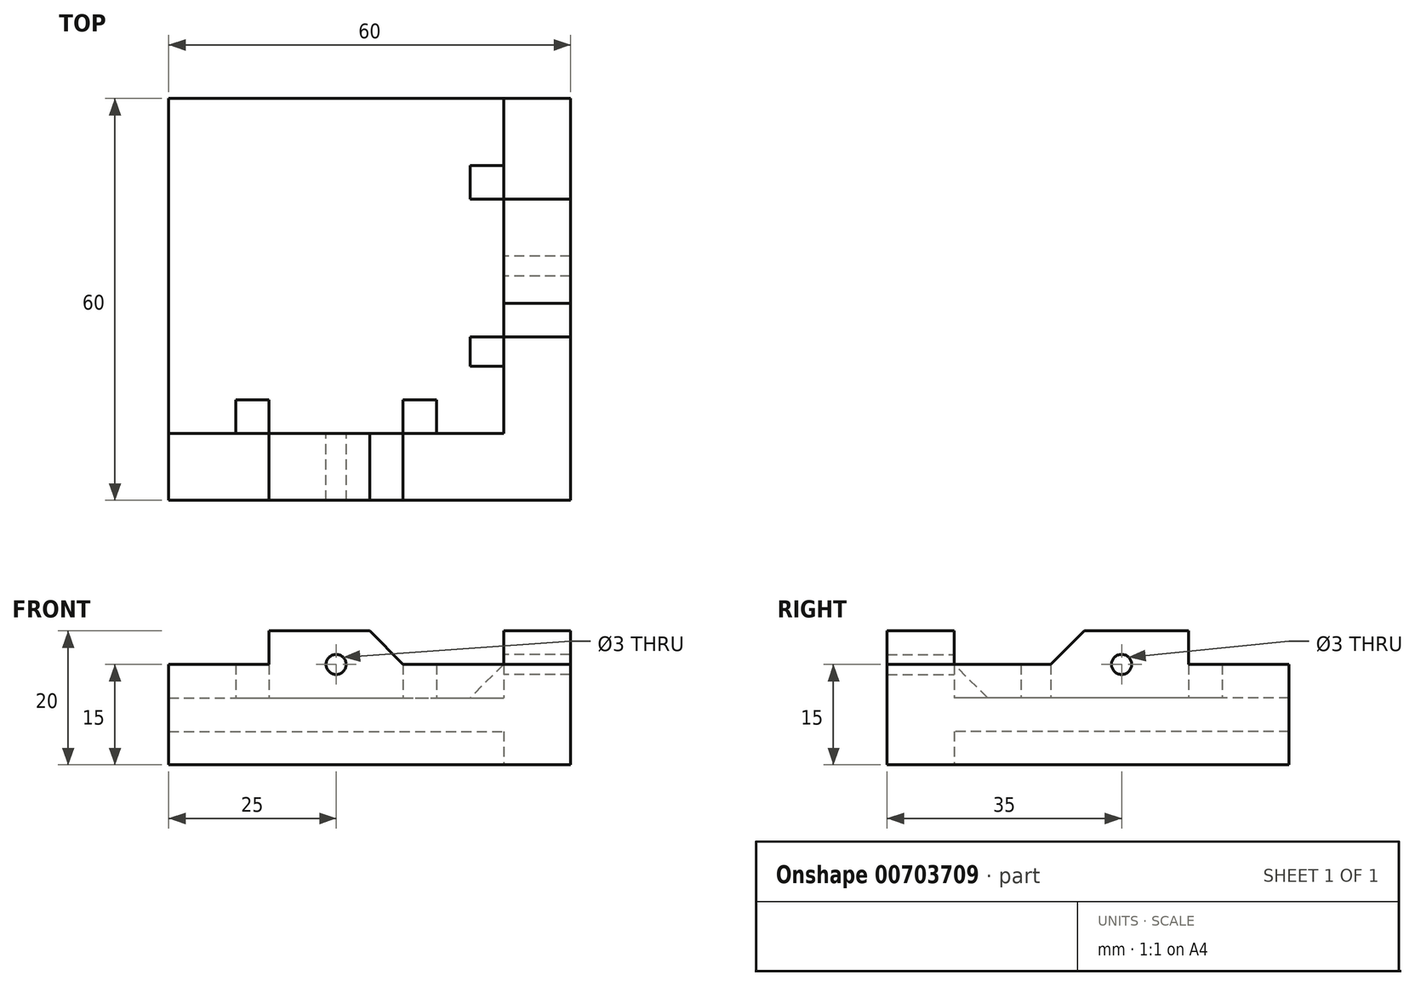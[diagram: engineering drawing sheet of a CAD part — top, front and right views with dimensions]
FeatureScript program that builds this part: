
annotation { "Feature Type Name" : "Feature", "Feature Type Description" : "" }
export const myFeature = defineFeature(function(context is Context, id is Id, definition is map)
    precondition{}
    {
        {
            var Q0;
            Q0=qCreatedBy(makeId("Top.planeOp"),FACE);
            var sketch = newSketch(context, id + "F0", { "sketchPlane" : qUnion([Q0])});
            skLineSegment(sketch, "E0", {"start": v(0, 0) * mm, "end": v(50, 0) * mm});
            skLineSegment(sketch, "E1", {"start": v(50, 0) * mm, "end": v(50, 50) * mm});
            skLineSegment(sketch, "E2.0", {"start": v(60, -10) * mm, "end": v(60, 50) * mm});
            skLineSegment(sketch, "E2.1", {"start": v(0, -10) * mm, "end": v(60, -10) * mm});
            skLineSegment(sketch, "E3", {"start": v(50, 50) * mm, "end": v(60, 50) * mm});
            skLineSegment(sketch, "E4", {"start": v(0, 0) * mm, "end": v(0, -10) * mm});
            skSolve(sketch);
        }
        {
            var Q0;
            Q0=makeQuery(id+"F0.imprint","IMPRINT",FACE,{"disambiguationData":[TD([[makeQuery(id+"F0.imprint","IMPRINT",EDGE,{"derivedFrom":sQuery(id+"F0.wireOp",EDGE,"E0")}),-1.0]])]});
            extrude(context, id + "F1", {"entities" : qUnion([Q0]), "depth" : 15 * mm, "offsetDistance" : 25 * mm});
        }
        {
            var Q0;
            Q0=makeQuery(id+"F1.opExtrude","SWEPT_FACE",FACE,{"disambiguationData":[OSD([sQuery(id+"F0.wireOp",EDGE,"E1")])]});
            var sketch = newSketch(context, id + "F2", { "sketchPlane" : qUnion([Q0])});
            skLineSegment(sketch, "E5", {"start": v(-50, 0) * mm, "end": v(-50, 5) * mm});
            skLineSegment(sketch, "E6", {"start": v(-50, 5) * mm, "end": v(0, 5) * mm});
            skLineSegment(sketch, "E7.0", {"start": v(-50, 10) * mm, "end": v(0, 10) * mm});
            skLineSegment(sketch, "E8", {"start": v(-50, 15) * mm, "end": v(-37.5, 15) * mm});
            skLineSegment(sketch, "E9", {"start": v(0, 15) * mm, "end": v(-12.5, 15) * mm});
            skLineSegment(sketch, "E10", {"start": v(-37.5, 15) * mm, "end": v(-35, 15) * mm});
            skLineSegment(sketch, "E11", {"start": v(-35, 15) * mm, "end": v(-35, 10) * mm});
            skLineSegment(sketch, "E12.0", {"start": v(-40, 15) * mm, "end": v(-40, 10) * mm});
            skLineSegment(sketch, "E13.0", {"start": v(-10, 15) * mm, "end": v(-10, 10) * mm});
            skLineSegment(sketch, "E14.0", {"start": v(-14.42, 15) * mm, "end": v(-14.42, 10) * mm});
            skLineSegment(sketch, "E15", {"start": v(-35, 15) * mm, "end": v(-35, 20) * mm});
            skLineSegment(sketch, "E16", {"start": v(-35, 20) * mm, "end": v(-19.42, 20) * mm});
            skLineSegment(sketch, "E17", {"start": v(-19.42, 20) * mm, "end": v(-14.42, 15) * mm});
            skCircle(sketch, "E18", {"center": v(-25, 15) * mm, "radius": 1.5 * mm});
            skSolve(sketch);
        }
        {
            var Q0;
            {var subQ0=sQuery(id+"F2.wireOp",EDGE,"E6");Q0=makeQuery(id+"F2.imprint","IMPRINT",FACE,{"disambiguationData":[TD([[makeQuery(id+"F2.imprint","IMPRINT",EDGE,{"derivedFrom":subQ0}),1.0]])]});}
            extrude(context, id + "F3", {"entities" : qUnion([Q0]), "operationType" : NewBodyOperationType.ADD, "depth" : 50 * mm, "offsetDistance" : 25 * mm});
        }
        {
            var Q0;
            {var subQ0=sQuery(id+"F2.wireOp",EDGE,"E10");Q0=makeQuery(id+"F2.imprint","IMPRINT",FACE,{"disambiguationData":[TD([[makeQuery(id+"F2.imprint","IMPRINT",EDGE,{"derivedFrom":subQ0}),1.0]])]});}
            var Q1;
            {var subQ0=sQuery(id+"F2.wireOp",EDGE,"E13.0");Q1=makeQuery(id+"F2.imprint","IMPRINT",FACE,{"disambiguationData":[TD([[makeQuery(id+"F2.imprint","IMPRINT",EDGE,{"derivedFrom":subQ0}),-1.0]])]});}
            extrude(context, id + "F4", {"entities" : qUnion([Q0, Q1]), "operationType" : NewBodyOperationType.ADD, "depth" : 5 * mm, "offsetDistance" : 25 * mm});
        }
        {
            var Q0;
            Q0=makeQuery(id+"F4.opExtrude","SWEPT_FACE",FACE,{"disambiguationData":[OSD([sQuery(id+"F2.wireOp",EDGE,"E12.0")])]});
            var sketch = newSketch(context, id + "F5", { "sketchPlane" : qUnion([Q0])});
            skLineSegment(sketch, "E19", {"start": v(-50, 15) * mm, "end": v(-45, 10) * mm});
            skLineSegment(sketch, "E20", {"start": v(-45, 10) * mm, "end": v(-45, 15) * mm});
            skLineSegment(sketch, "E21", {"start": v(-45, 15) * mm, "end": v(-50, 15) * mm});
            skSolve(sketch);
        }
        {
            var Q0;
            Q0 = qSketchRegion(id + "F5", true);
            extrude(context, id + "F6", {"entities" : qUnion([Q0]), "operationType" : NewBodyOperationType.REMOVE, "oppositeDirection" : true, "depth" : 34.1 * mm, "offsetDistance" : 25 * mm});
        }
        {
            var Q0;
            {var subQ0=sQuery(id+"F2.wireOp",EDGE,"E7.0");var subQ3=sQuery(id+"F0.wireOp",EDGE,"E0");Q0=makeQuery(id+"F3.boolean.opBoolean","SPLIT",FACE,{"disambiguationData":[TD([makeQuery(id+"F3.opExtrude","SWEPT_FACE",FACE,{"disambiguationData":[OSD([subQ0])]})])],"derivedFrom":makeQuery(id+"F1.opExtrude","SWEPT_FACE",FACE,{"disambiguationData":[OSD([subQ3])]})});}
            var sketch = newSketch(context, id + "F7", { "sketchPlane" : qUnion([Q0])});
            skLineSegment(sketch, "E22", {"start": v(-50, 0) * mm, "end": v(-50, 5) * mm});
            skLineSegment(sketch, "E23", {"start": v(-50, 5) * mm, "end": v(0, 5) * mm});
            skLineSegment(sketch, "E24.0", {"start": v(-50, 10) * mm, "end": v(0, 10) * mm});
            skLineSegment(sketch, "E25", {"start": v(-50, 15) * mm, "end": v(-37.5, 15) * mm});
            skLineSegment(sketch, "E26", {"start": v(0, 15) * mm, "end": v(-12.5, 15) * mm});
            skLineSegment(sketch, "E27", {"start": v(-37.5, 15) * mm, "end": v(-35, 15) * mm});
            skLineSegment(sketch, "E28", {"start": v(-35, 15) * mm, "end": v(-35, 10) * mm});
            skLineSegment(sketch, "E29.0", {"start": v(-40, 15) * mm, "end": v(-40, 10) * mm});
            skLineSegment(sketch, "E30.0", {"start": v(-10, 15) * mm, "end": v(-10, 10) * mm});
            skLineSegment(sketch, "E31.0", {"start": v(-15, 15) * mm, "end": v(-15, 10) * mm});
            skLineSegment(sketch, "E32", {"start": v(-15, 15) * mm, "end": v(-15, 20) * mm});
            skLineSegment(sketch, "E33", {"start": v(-15, 20) * mm, "end": v(-30, 20) * mm});
            skCircle(sketch, "E34", {"center": v(-25, 15) * mm, "radius": 1.5 * mm});
            skLineSegment(sketch, "E35", {"start": v(-30, 20) * mm, "end": v(-35, 15) * mm});
            skSolve(sketch);
        }
        {
            var Q0;
            {var subQ0=sQuery(id+"F7.wireOp",EDGE,"E27");Q0=makeQuery(id+"F7.imprint","IMPRINT",FACE,{"disambiguationData":[TD([[makeQuery(id+"F7.imprint","IMPRINT",EDGE,{"derivedFrom":subQ0}),1.0]])]});}
            var Q1;
            {var subQ0=sQuery(id+"F7.wireOp",EDGE,"E30.0");Q1=makeQuery(id+"F7.imprint","IMPRINT",FACE,{"disambiguationData":[TD([[makeQuery(id+"F7.imprint","IMPRINT",EDGE,{"derivedFrom":subQ0}),-1.0]])]});}
            extrude(context, id + "F8", {"entities" : qUnion([Q0, Q1]), "operationType" : NewBodyOperationType.ADD, "depth" : 5 * mm, "offsetDistance" : 25 * mm});
        }
        {
            var Q0;
            Q0=makeQuery(id+"F8.opExtrude","SWEPT_FACE",FACE,{"disambiguationData":[OSD([sQuery(id+"F7.wireOp",EDGE,"E30.0")])]});
            var sketch = newSketch(context, id + "F9", { "sketchPlane" : qUnion([Q0])});
            skLineSegment(sketch, "E36", {"start": v(-5, 10) * mm, "end": v(0, 15) * mm});
            skLineSegment(sketch, "E37", {"start": v(0, 15) * mm, "end": v(-5, 15) * mm});
            skLineSegment(sketch, "E38", {"start": v(-5, 15) * mm, "end": v(-5, 10) * mm});
            skSolve(sketch);
        }
        {
            var Q0;
            Q0=makeQuery(id+"F9.imprint","IMPRINT",FACE,{"disambiguationData":[TD([[makeQuery(id+"F9.imprint","IMPRINT",EDGE,{"derivedFrom":sQuery(id+"F9.wireOp",EDGE,"E36")}),1.0]])]});
            extrude(context, id + "F10", {"entities" : qUnion([Q0]), "operationType" : NewBodyOperationType.REMOVE, "oppositeDirection" : true, "depth" : 37.3 * mm, "offsetDistance" : 25 * mm});
        }
        {
            var Q0;
            {var subQ0=sQuery(id+"F2.wireOp",EDGE,"E15");Q0=makeQuery(id+"F2.imprint","IMPRINT",FACE,{"disambiguationData":[TD([[makeQuery(id+"F2.imprint","IMPRINT",EDGE,{"derivedFrom":subQ0}),-1.0]])]});}
            extrude(context, id + "F11", {"entities" : qUnion([Q0]), "operationType" : NewBodyOperationType.ADD, "oppositeDirection" : true, "depth" : 10 * mm, "offsetDistance" : 25 * mm});
        }
        {
            var Q0;
            {var subQ0=sQuery(id+"F7.wireOp",EDGE,"E32");Q0=makeQuery(id+"F7.imprint","IMPRINT",FACE,{"disambiguationData":[TD([[makeQuery(id+"F7.imprint","IMPRINT",EDGE,{"derivedFrom":subQ0}),1.0]])]});}
            extrude(context, id + "F12", {"entities" : qUnion([Q0]), "operationType" : NewBodyOperationType.ADD, "oppositeDirection" : true, "depth" : 10 * mm, "offsetDistance" : 25 * mm});
        }
        {
            var Q0;
            {var subQ0=sQuery(id+"F2.wireOp",EDGE,"E18");var subQ1=makeQuery(id+"F1.opExtrude","CAP_EDGE",EDGE,{"disambiguationData":[OSD([sQuery(id+"F0.wireOp",EDGE,"E1")])],"isStart":false});var subQ2=makeQuery(id+"F2.imprint","INTERSECT",VERTEX,{"disambiguationData":[OD(0.0)],"derivedFrom":[subQ1,subQ0]});Q0=makeQuery(id+"F2.imprint","IMPRINT",FACE,{"disambiguationData":[TD([[makeQuery(id+"F2.imprint","IMPRINT",EDGE,{"disambiguationData":[TD([[subQ2,1.0]])],"derivedFrom":subQ0}),1.0]])]});}
            var Q1;
            {var subQ0=sQuery(id+"F2.wireOp",EDGE,"E18");var subQ1=makeQuery(id+"F1.opExtrude","CAP_EDGE",EDGE,{"disambiguationData":[OSD([sQuery(id+"F0.wireOp",EDGE,"E1")])],"isStart":false});var subQ2=makeQuery(id+"F2.imprint","INTERSECT",VERTEX,{"disambiguationData":[OD(0.0)],"derivedFrom":[subQ1,subQ0]});Q1=makeQuery(id+"F2.imprint","IMPRINT",FACE,{"disambiguationData":[TD([[makeQuery(id+"F2.imprint","IMPRINT",EDGE,{"disambiguationData":[TD([[subQ2,-1.0]])],"derivedFrom":subQ0}),1.0]])]});}
            extrude(context, id + "F13", {"entities" : qUnion([Q0, Q1]), "operationType" : NewBodyOperationType.REMOVE, "oppositeDirection" : true, "depth" : 25 * mm, "offsetDistance" : 25 * mm});
        }
        {
            var Q0;
            {var subQ0=sQuery(id+"F7.wireOp",EDGE,"E34");var subQ1=makeQuery(id+"F1.opExtrude","CAP_EDGE",EDGE,{"disambiguationData":[OSD([sQuery(id+"F0.wireOp",EDGE,"E0")])],"isStart":false});var subQ2=makeQuery(id+"F7.imprint","INTERSECT",VERTEX,{"disambiguationData":[OD(0.0)],"derivedFrom":[subQ1,subQ0]});Q0=makeQuery(id+"F7.imprint","IMPRINT",FACE,{"disambiguationData":[TD([[makeQuery(id+"F7.imprint","IMPRINT",EDGE,{"disambiguationData":[TD([[subQ2,-1.0]])],"derivedFrom":subQ0}),1.0]])]});}
            var Q1;
            {var subQ0=sQuery(id+"F7.wireOp",EDGE,"E34");var subQ1=makeQuery(id+"F1.opExtrude","CAP_EDGE",EDGE,{"disambiguationData":[OSD([sQuery(id+"F0.wireOp",EDGE,"E0")])],"isStart":false});var subQ2=makeQuery(id+"F7.imprint","INTERSECT",VERTEX,{"disambiguationData":[OD(0.0)],"derivedFrom":[subQ1,subQ0]});Q1=makeQuery(id+"F7.imprint","IMPRINT",FACE,{"disambiguationData":[TD([[makeQuery(id+"F7.imprint","IMPRINT",EDGE,{"disambiguationData":[TD([[subQ2,1.0]])],"derivedFrom":subQ0}),1.0]])]});}
            extrude(context, id + "F14", {"entities" : qUnion([Q0, Q1]), "operationType" : NewBodyOperationType.REMOVE, "oppositeDirection" : true, "depth" : 25 * mm, "offsetDistance" : 25 * mm});
        }
    });
